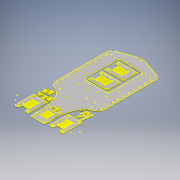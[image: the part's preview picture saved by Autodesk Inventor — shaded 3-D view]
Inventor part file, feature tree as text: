
AUTODESK INVENTOR PART (.ipt)
format: ipt  version: 2016 (Build 200138000, 138)  size: 2,419,712 bytes
history: native  units: in
note: dims shown in document units (in); Inventor stores cm internally (conversion verified against a paired STEP export)
features: projected_geometry x12, sketch x6, extrude x5, pattern_linear x1
ambient origin geometry x8: Origin, YZ Plane, XZ Plane, XY Plane, X Axis, Y Axis, Z Axis, Center Point
bodies: Solid1 (feature_tree), Solid2 (feature_tree)
feature tree (24):
  extrude  "Extrusion1"  Depth=1.0in TaperAngle=0.0deg
  extrude  "Extrusion3"  Depth=1.0in TaperAngle=0.0deg
  extrude  "Extrusion4"  Depth=1.0in TaperAngle=0.0deg
  extrude  "Extrusion5"  [1 undecoded]
  sketch  "Sketch7"
  extrude  "Extrusion2"  [1 undecoded]
  pattern_linear  "Rectangular Pattern1"  [2 undecoded]
  sketch  "Sketch1"  dims[d0=0.125in d1=0.0in d2=1.0in d3=0.0in]
  sketch  "Sketch3"  dims[d4=1.1811in d6=2.6in d7=1.0in d8=0.0in]
  sketch  "Sketch4"  dims[d9=0.1562in d10=1.0in d11=0.0in]
  sketch  "Sketch5"  dims[d14=1.0in d15=0.0in]
  sketch  "Sketch6"
  projected_geometry  "Projected Loop6"
  projected_geometry  "Projected Loop7"
  projected_geometry  "Projected Loop8"
  projected_geometry  "Projected Loop9"
  projected_geometry  "Projected Loop10"
  projected_geometry  "Projected Loop11"
  projected_geometry  "Projected Loop12"
  projected_geometry  "Projected Loop13"
  projected_geometry  "Projected Loop14"
  projected_geometry  "Projected Loop15"
  projected_geometry  "Projected Loop16"
  projected_geometry  "Projected Loop17"
note: 4 required parameter values undecoded (feature->parameter linkage not recoverable at this tier; creation-order binding heuristic only, values carry confidence <= 0.55)
